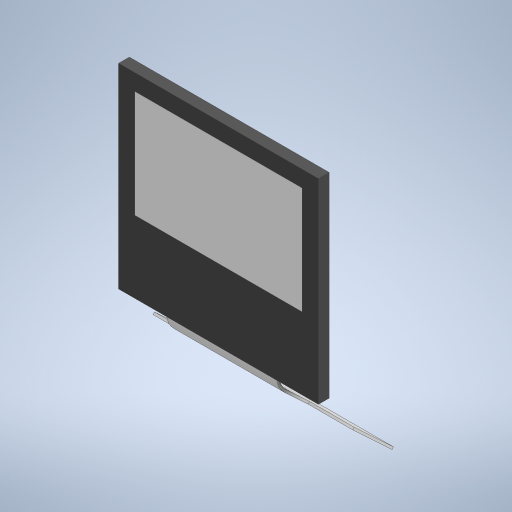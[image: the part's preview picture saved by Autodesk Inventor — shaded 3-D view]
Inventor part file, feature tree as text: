
AUTODESK INVENTOR PART (.ipt)
format: ipt  version: 2023 (Build 270158000, 158)  size: 290,816 bytes
history: native  units: mm
features: sketch x5, extrude x4, plane x2, projected_geometry x1
ambient origin geometry x8: Origin, YZ Plane, XZ Plane, XY Plane, X Axis, Y Axis, Z Axis, Center Point
bodies: Solid1 (feature_tree)
feature tree (12):
  extrude  "Extrusion1"  Depth=18.2mm
  plane  "Work Plane1"
  sketch  "Sketch5"  dims[d2=1.0mm d3=0.0mm d4=-0.25mm]
  plane  "Work Plane2"
  extrude  "Extrusion4"  [1 undecoded]
  extrude  "Extrusion5"  Depth=1.5mm
  extrude  "Extrusion6"  Depth=2.0mm
  sketch  "Sketch2"  dims[d0=18.6mm d1=18.2mm]
  sketch  "Sketch7"  dims[d13=10.0mm d15=1.5mm]
  sketch  "Sketch8"  dims[d16=1.5mm d19=2.0mm]
  projected_geometry  "Projected Loop1"
  sketch  "Sketch9"  dims[d22=7.504916mm d23=0.5mm d24=0.2mm d26=10.3mm d27=0.0mm d28=5.0mm d29=18.6mm d30=0.0mm d31=0.01mm d32=0.0mm d33=8.0mm]
note: 1 required parameter value undecoded (feature->parameter linkage not recoverable at this tier; creation-order binding heuristic only, values carry confidence <= 0.55)
